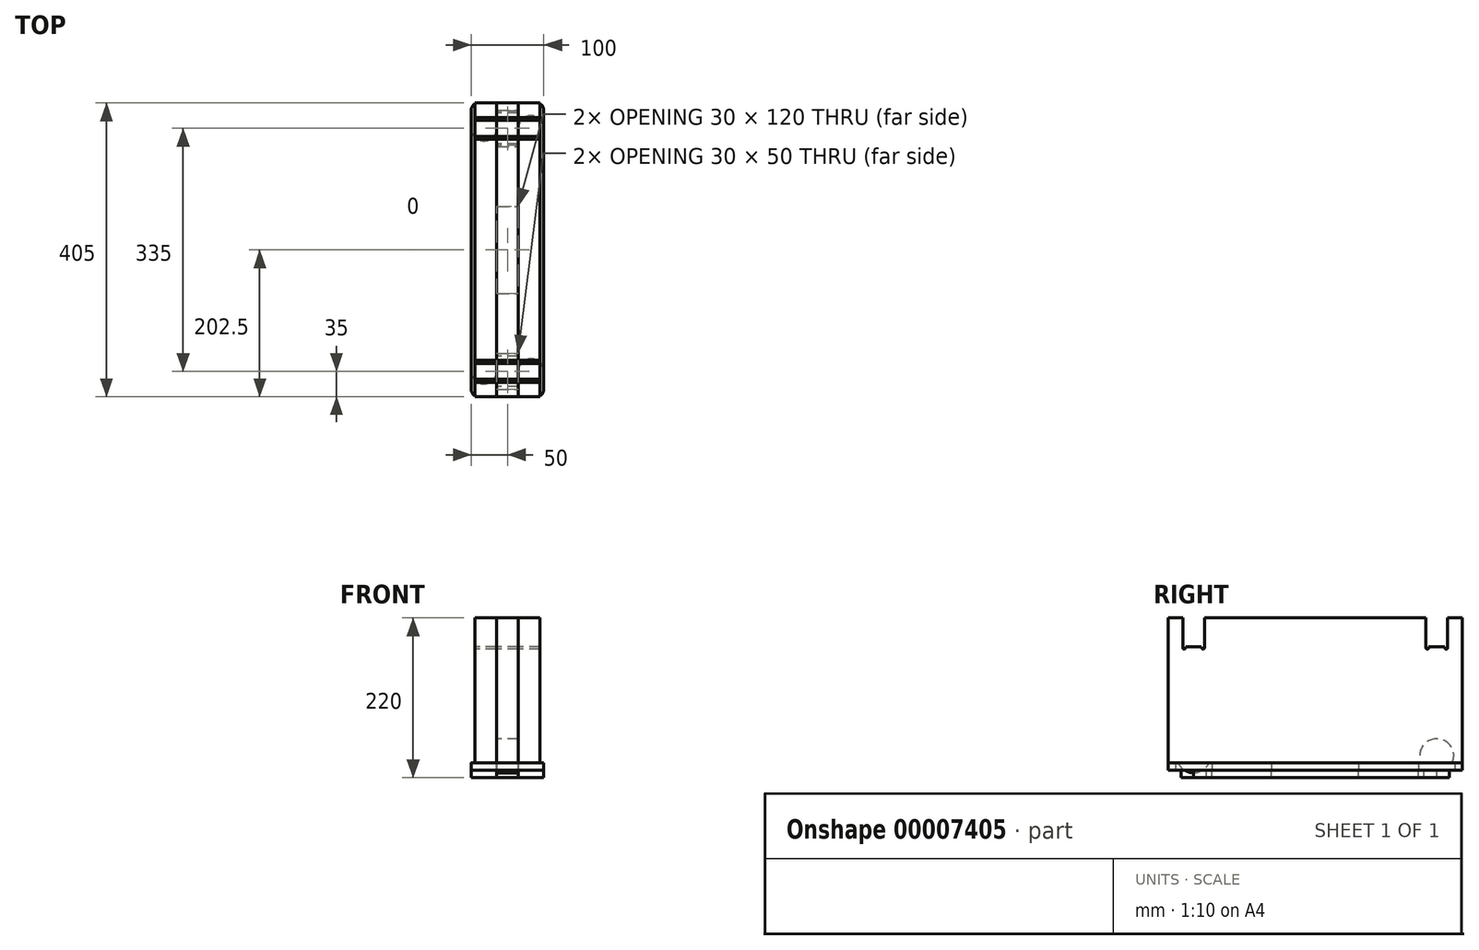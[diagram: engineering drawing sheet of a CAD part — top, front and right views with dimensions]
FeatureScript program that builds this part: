
annotation { "Feature Type Name" : "Feature", "Feature Type Description" : "" }
export const myFeature = defineFeature(function(context is Context, id is Id, definition is map)
    precondition{}
    {
        {
            var Q0;
            Q0=qCreatedBy(makeId("Top.planeOp"),FACE);
            var sketch = newSketch(context, id + "F0", { "sketchPlane" : qUnion([Q0])});
            skLineSegment(sketch, "E0.bottom", {"start": v(10, 0) * mm, "end": v(90, 0) * mm});
            skLineSegment(sketch, "E0.top", {"start": v(10, 405) * mm, "end": v(90, 405) * mm});
            skLineSegment(sketch, "E0.left", {"start": v(0, 10) * mm, "end": v(0, 395) * mm});
            skLineSegment(sketch, "E0.right", {"start": v(100, 10) * mm, "end": v(100, 395) * mm});
            skLineSegment(sketch, "E1", {"start": v(35, 0) * mm, "end": v(35, 405) * mm, "construction": true});
            skLineSegment(sketch, "E2", {"start": v(65, 0) * mm, "end": v(65, 405) * mm, "construction": true});
            skLineSegment(sketch, "E3", {"start": v(0, 202.5) * mm, "end": v(35, 202.5) * mm, "construction": true});
            skLineSegment(sketch, "E4", {"start": v(65, 202.5) * mm, "end": v(100, 202.5) * mm, "construction": true});
            skLineSegment(sketch, "E5.bottom", {"start": v(37, 395) * mm, "end": v(63, 395) * mm});
            skLineSegment(sketch, "E5.top", {"start": v(37, 345) * mm, "end": v(63, 345) * mm});
            skLineSegment(sketch, "E5.left", {"start": v(35, 393) * mm, "end": v(35, 347) * mm});
            skLineSegment(sketch, "E5.right", {"start": v(65, 393) * mm, "end": v(65, 347) * mm});
            skLineSegment(sketch, "E6", {"start": v(35, 202.5) * mm, "end": v(35, 260.5) * mm});
            skLineSegment(sketch, "E7", {"start": v(37, 262.5) * mm, "end": v(63, 262.5) * mm});
            skLineSegment(sketch, "E8", {"start": v(65, 260.5) * mm, "end": v(65, 202.5) * mm});
            skPoint(sketch, "E9.visualSharp", {"position": v(35, 395) * mm});
            skArc(sketch, "E9.filletArc", {"start": v(37, 395) * mm, "mid": v(35.59, 394.41) * mm, "end": v(35, 393) * mm});
            skPoint(sketch, "E10.visualSharp", {"position": v(35, 345) * mm});
            skArc(sketch, "E10.filletArc", {"start": v(35, 347) * mm, "mid": v(35.59, 345.59) * mm, "end": v(37, 345) * mm});
            skPoint(sketch, "E11.visualSharp", {"position": v(65, 395) * mm});
            skArc(sketch, "E11.filletArc", {"start": v(65, 393) * mm, "mid": v(64.41, 394.41) * mm, "end": v(63, 395) * mm});
            skPoint(sketch, "E12.visualSharp", {"position": v(65, 345) * mm});
            skArc(sketch, "E12.filletArc", {"start": v(63, 345) * mm, "mid": v(64.41, 345.59) * mm, "end": v(65, 347) * mm});
            skPoint(sketch, "E13.visualSharp", {"position": v(35, 262.5) * mm});
            skArc(sketch, "E13.filletArc", {"start": v(37, 262.5) * mm, "mid": v(35.59, 261.91) * mm, "end": v(35, 260.5) * mm});
            skPoint(sketch, "E14.visualSharp", {"position": v(65, 262.5) * mm});
            skArc(sketch, "E14.filletArc", {"start": v(65, 260.5) * mm, "mid": v(64.41, 261.91) * mm, "end": v(63, 262.5) * mm});
            skArc(sketch, "E15.0.MirrorCS", {"start": v(63, 60) * mm, "mid": v(64.41, 59.41) * mm, "end": v(65, 58) * mm});
            skArc(sketch, "E15.1.MirrorCS", {"start": v(65, 144.5) * mm, "mid": v(64.41, 143.09) * mm, "end": v(63, 142.5) * mm});
            skArc(sketch, "E15.2.MirrorCS", {"start": v(37, 10) * mm, "mid": v(35.59, 10.59) * mm, "end": v(35, 12) * mm});
            skArc(sketch, "E15.3.MirrorCS", {"start": v(35, 58) * mm, "mid": v(35.59, 59.41) * mm, "end": v(37, 60) * mm});
            skArc(sketch, "E15.4.MirrorCS", {"start": v(37, 142.5) * mm, "mid": v(35.59, 143.09) * mm, "end": v(35, 144.5) * mm});
            skArc(sketch, "E15.5.MirrorCS", {"start": v(65, 12) * mm, "mid": v(64.41, 10.59) * mm, "end": v(63, 10) * mm});
            skPoint(sketch, "E15.6.MirrorP", {"position": v(65, 10) * mm});
            skLineSegment(sketch, "E15.7.MirrorCS", {"start": v(37, 142.5) * mm, "end": v(63, 142.5) * mm});
            skPoint(sketch, "E15.8.MirrorP", {"position": v(35, 10) * mm});
            skLineSegment(sketch, "E15.9.MirrorCS", {"start": v(35, 12) * mm, "end": v(35, 58) * mm});
            skPoint(sketch, "E15.10.MirrorP", {"position": v(65, 142.5) * mm});
            skLineSegment(sketch, "E15.11.MirrorCS", {"start": v(37, 60) * mm, "end": v(63, 60) * mm});
            skLineSegment(sketch, "E15.12.MirrorCS", {"start": v(37, 10) * mm, "end": v(63, 10) * mm});
            skLineSegment(sketch, "E15.13.MirrorCS", {"start": v(65, 12) * mm, "end": v(65, 58) * mm});
            skPoint(sketch, "E15.14.MirrorP", {"position": v(35, 142.5) * mm});
            skPoint(sketch, "E15.15.MirrorP", {"position": v(35, 60) * mm});
            skPoint(sketch, "E15.16.MirrorP", {"position": v(65, 60) * mm});
            skLineSegment(sketch, "E16.0.MirrorCS", {"start": v(35, 202.5) * mm, "end": v(35, 144.5) * mm});
            skLineSegment(sketch, "E17.0.MirrorCS", {"start": v(65, 144.5) * mm, "end": v(65, 202.5) * mm});
            skPoint(sketch, "E18.visualSharp", {"position": v(0, 405) * mm});
            skArc(sketch, "E18.filletArc", {"start": v(10, 405) * mm, "mid": v(2.93, 402.07) * mm, "end": v(0, 395) * mm});
            skPoint(sketch, "E19.visualSharp", {"position": v(100, 405) * mm});
            skArc(sketch, "E19.filletArc", {"start": v(100, 395) * mm, "mid": v(97.07, 402.07) * mm, "end": v(90, 405) * mm});
            skPoint(sketch, "E20.visualSharp", {"position": v(100, 0) * mm});
            skArc(sketch, "E20.filletArc", {"start": v(90, 0) * mm, "mid": v(97.07, 2.93) * mm, "end": v(100, 10) * mm});
            skPoint(sketch, "E21.visualSharp", {"position": v(0, 0) * mm});
            skArc(sketch, "E21.filletArc", {"start": v(0, 10) * mm, "mid": v(2.93, 2.93) * mm, "end": v(10, 0) * mm});
            skSolve(sketch);
        }
        {
            var Q0;
            Q0=makeQuery(id+"F0.imprint","IMPRINT",FACE,{"disambiguationData":[TD([[makeQuery(id+"F0.imprint","IMPRINT",EDGE,{"derivedFrom":sQuery(id+"F0.wireOp",EDGE,"E0.bottom")}),1.0]])]});
            extrude(context, id + "F1", {"entities" : qUnion([Q0]), "depth" : 10 * mm});
        }
        {
            var Q0;
            Q0=makeQuery(id+"F1.opExtrude","CAP_FACE",FACE,{"disambiguationData":[OSD([sQuery(id+"F0.wireOp",EDGE,"E0.bottom"),sQuery(id+"F0.wireOp",EDGE,"E0.top"),sQuery(id+"F0.wireOp",EDGE,"E0.left"),sQuery(id+"F0.wireOp",EDGE,"E0.right"),sQuery(id+"F0.wireOp",EDGE,"E5.bottom"),sQuery(id+"F0.wireOp",EDGE,"E5.top"),sQuery(id+"F0.wireOp",EDGE,"E5.left"),sQuery(id+"F0.wireOp",EDGE,"E5.right"),sQuery(id+"F0.wireOp",EDGE,"E6"),sQuery(id+"F0.wireOp",EDGE,"E7"),sQuery(id+"F0.wireOp",EDGE,"E8"),sQuery(id+"F0.wireOp",EDGE,"E9.filletArc"),sQuery(id+"F0.wireOp",EDGE,"E10.filletArc"),sQuery(id+"F0.wireOp",EDGE,"E11.filletArc"),sQuery(id+"F0.wireOp",EDGE,"E12.filletArc"),sQuery(id+"F0.wireOp",EDGE,"E13.filletArc"),sQuery(id+"F0.wireOp",EDGE,"E14.filletArc"),sQuery(id+"F0.wireOp",EDGE,"E15.0.MirrorCS"),sQuery(id+"F0.wireOp",EDGE,"E15.1.MirrorCS"),sQuery(id+"F0.wireOp",EDGE,"E15.2.MirrorCS"),sQuery(id+"F0.wireOp",EDGE,"E15.3.MirrorCS"),sQuery(id+"F0.wireOp",EDGE,"E15.4.MirrorCS"),sQuery(id+"F0.wireOp",EDGE,"E15.5.MirrorCS"),sQuery(id+"F0.wireOp",EDGE,"E15.7.MirrorCS"),sQuery(id+"F0.wireOp",EDGE,"E15.9.MirrorCS"),sQuery(id+"F0.wireOp",EDGE,"E15.11.MirrorCS"),sQuery(id+"F0.wireOp",EDGE,"E15.12.MirrorCS"),sQuery(id+"F0.wireOp",EDGE,"E15.13.MirrorCS"),sQuery(id+"F0.wireOp",EDGE,"E16.0.MirrorCS"),sQuery(id+"F0.wireOp",EDGE,"E17.0.MirrorCS"),sQuery(id+"F0.wireOp",EDGE,"E18.filletArc"),sQuery(id+"F0.wireOp",EDGE,"E19.filletArc"),sQuery(id+"F0.wireOp",EDGE,"E20.filletArc"),sQuery(id+"F0.wireOp",EDGE,"E21.filletArc")])],"isStart":false});
            var sketch = newSketch(context, id + "F2", { "sketchPlane" : qUnion([Q0])});
            skLineSegment(sketch, "E22.bottom", {"start": v(35, 0) * mm, "end": v(5, 0) * mm});
            skLineSegment(sketch, "E22.top", {"start": v(35, 405) * mm, "end": v(5, 405) * mm});
            skLineSegment(sketch, "E22.left", {"start": v(35, 0) * mm, "end": v(35, 405) * mm});
            skLineSegment(sketch, "E22.right", {"start": v(5, 0) * mm, "end": v(5, 405) * mm});
            skLineSegment(sketch, "E23.bottom", {"start": v(65, 0) * mm, "end": v(95, 0) * mm});
            skLineSegment(sketch, "E23.top", {"start": v(65, 405) * mm, "end": v(95, 405) * mm});
            skLineSegment(sketch, "E23.left", {"start": v(65, 0) * mm, "end": v(65, 405) * mm});
            skLineSegment(sketch, "E23.right", {"start": v(95, 0) * mm, "end": v(95, 405) * mm});
            skSolve(sketch);
        }
        {
            var Q0;
            {var subQ9=sQuery(id+"F2.wireOp",EDGE,"E22.left");var subQ12=makeQuery(id+"F2.imprint","INTERSECT",VERTEX,{"derivedFrom":[makeQuery(id+"F1.opExtrude","CAP_EDGE",EDGE,{"disambiguationData":[OSD([sQuery(id+"F0.wireOp",EDGE,"E13.filletArc")])],"isStart":false}),subQ9]});var subQ16=makeQuery(id+"F2.imprint","INTERSECT",VERTEX,{"derivedFrom":[makeQuery(id+"F1.opExtrude","CAP_EDGE",EDGE,{"disambiguationData":[OSD([sQuery(id+"F0.wireOp",EDGE,"E15.4.MirrorCS")])],"isStart":false}),subQ9]});Q0=makeQuery(id+"F2.imprint","IMPRINT",FACE,{"disambiguationData":[TD([[makeQuery(id+"F2.imprint","IMPRINT",EDGE,{"disambiguationData":[TD([[subQ12,-1.0],[subQ16,1.0]])],"derivedFrom":subQ9}),-1.0]])]});}
            var Q1;
            {var subQ7=sQuery(id+"F2.wireOp",EDGE,"E23.left");var subQ9=makeQuery(id+"F2.imprint","INTERSECT",VERTEX,{"derivedFrom":[makeQuery(id+"F1.opExtrude","CAP_EDGE",EDGE,{"disambiguationData":[OSD([sQuery(id+"F0.wireOp",EDGE,"E11.filletArc")])],"isStart":false}),subQ7]});var subQ11=makeQuery(id+"F2.imprint","INTERSECT",VERTEX,{"derivedFrom":[makeQuery(id+"F1.opExtrude","CAP_EDGE",EDGE,{"disambiguationData":[OSD([sQuery(id+"F0.wireOp",EDGE,"E12.filletArc")])],"isStart":false}),subQ7]});Q1=makeQuery(id+"F2.imprint","IMPRINT",FACE,{"disambiguationData":[TD([[makeQuery(id+"F2.imprint","IMPRINT",EDGE,{"disambiguationData":[TD([[subQ9,-1.0],[subQ11,1.0]])],"derivedFrom":subQ7}),1.0]])]});}
            var Q2;
            {var subQ0=makeQuery(id+"F1.opExtrude","CAP_EDGE",EDGE,{"disambiguationData":[OSD([sQuery(id+"F0.wireOp",EDGE,"E20.filletArc")])],"isStart":false});var subQ3=sQuery(id+"F2.wireOp",EDGE,"E23.bottom");var subQ4=makeQuery(id+"F2.imprint","INTERSECT",VERTEX,{"derivedFrom":[subQ0,subQ3]});Q2=makeQuery(id+"F2.imprint","IMPRINT",FACE,{"disambiguationData":[TD([[makeQuery(id+"F2.imprint","IMPRINT",EDGE,{"disambiguationData":[TD([[subQ4,-1.0]])],"derivedFrom":subQ3}),1.0]])]});}
            var Q3;
            {var subQ1=sQuery(id+"F2.wireOp",EDGE,"E22.right");var subQ3=sQuery(id+"F2.wireOp",EDGE,"E22.bottom");var subQ5=makeQuery(id+"F2.imprint","INTERSECT",VERTEX,{"derivedFrom":[subQ3,subQ1]});Q3=makeQuery(id+"F2.imprint","IMPRINT",FACE,{"disambiguationData":[TD([[makeQuery(id+"F2.imprint","IMPRINT",EDGE,{"disambiguationData":[TD([[subQ5,1.0]])],"derivedFrom":subQ3}),-1.0]])]});}
            var Q4;
            {var subQ0=makeQuery(id+"F1.opExtrude","CAP_EDGE",EDGE,{"disambiguationData":[OSD([sQuery(id+"F0.wireOp",EDGE,"E19.filletArc")])],"isStart":false});var subQ3=sQuery(id+"F2.wireOp",EDGE,"E23.top");var subQ4=makeQuery(id+"F2.imprint","INTERSECT",VERTEX,{"derivedFrom":[subQ0,subQ3]});Q4=makeQuery(id+"F2.imprint","IMPRINT",FACE,{"disambiguationData":[TD([[makeQuery(id+"F2.imprint","IMPRINT",EDGE,{"disambiguationData":[TD([[subQ4,-1.0]])],"derivedFrom":subQ3}),-1.0]])]});}
            var Q5;
            {var subQ1=sQuery(id+"F2.wireOp",EDGE,"E22.right");var subQ3=sQuery(id+"F2.wireOp",EDGE,"E22.top");var subQ5=makeQuery(id+"F2.imprint","INTERSECT",VERTEX,{"derivedFrom":[subQ3,subQ1]});Q5=makeQuery(id+"F2.imprint","IMPRINT",FACE,{"disambiguationData":[TD([[makeQuery(id+"F2.imprint","IMPRINT",EDGE,{"disambiguationData":[TD([[subQ5,1.0]])],"derivedFrom":subQ3}),1.0]])]});}
            extrude(context, id + "F3", {"entities" : qUnion([Q0, Q1, Q2, Q3, Q4, Q5]), "depth" : 200 * mm});
        }
        {
            var Q0;
            Q0=makeQuery(id+"F3.opExtrude","SWEPT_FACE",FACE,{"disambiguationData":[OSD([sQuery(id+"F2.wireOp",EDGE,"E22.left")])]});
            var sketch = newSketch(context, id + "F4", { "sketchPlane" : qUnion([Q0])});
            skCircle(sketch, "E24", {"center": v(35, 20) * mm, "radius": 23.5 * mm});
            skLineSegment(sketch, "E25.0", {"start": v(12, 10) * mm, "end": v(58, 10) * mm, "construction": true});
            skLineSegment(sketch, "E26", {"start": v(35, 20) * mm, "end": v(35, 10) * mm, "construction": true});
            skLineSegment(sketch, "E27", {"start": v(202.5, 10) * mm, "end": v(202.5, 210) * mm, "construction": true});
            skCircle(sketch, "E28.0.MirrorC", {"center": v(370, 20) * mm, "radius": 23.5 * mm});
            skSolve(sketch);
        }
        {
            var Q0;
            {var subQ0=makeQuery(id+"F3.opExtrude","CAP_EDGE",EDGE,{"disambiguationData":[OSD([sQuery(id+"F2.wireOp",EDGE,"E22.left")])],"isStart":true});var subQ1=sQuery(id+"F4.wireOp",EDGE,"E24");var subQ3=makeQuery(id+"F4.imprint","INTERSECT",VERTEX,{"disambiguationData":[OD(0.0)],"derivedFrom":[subQ0,subQ1]});Q0=makeQuery(id+"F4.imprint","IMPRINT",FACE,{"disambiguationData":[TD([[makeQuery(id+"F4.imprint","IMPRINT",EDGE,{"disambiguationData":[TD([[subQ3,1.0]])],"derivedFrom":subQ1}),1.0]])]});}
            var Q1;
            {var subQ0=makeQuery(id+"F3.opExtrude","CAP_EDGE",EDGE,{"disambiguationData":[OSD([sQuery(id+"F2.wireOp",EDGE,"E22.left")])],"isStart":true});var subQ1=sQuery(id+"F4.wireOp",EDGE,"E28.0.MirrorC");var subQ3=makeQuery(id+"F4.imprint","INTERSECT",VERTEX,{"disambiguationData":[OD(0.0)],"derivedFrom":[subQ0,subQ1]});Q1=makeQuery(id+"F4.imprint","IMPRINT",FACE,{"disambiguationData":[TD([[makeQuery(id+"F4.imprint","IMPRINT",EDGE,{"disambiguationData":[TD([[subQ3,1.0]])],"derivedFrom":subQ1}),-1.0]])]});}
            var Q2;
            {var subQ0=makeQuery(id+"F3.opExtrude","CAP_EDGE",EDGE,{"disambiguationData":[OSD([sQuery(id+"F2.wireOp",EDGE,"E22.left")])],"isStart":true});var subQ1=sQuery(id+"F4.wireOp",EDGE,"E24");var subQ3=makeQuery(id+"F4.imprint","INTERSECT",VERTEX,{"disambiguationData":[OD(0.0)],"derivedFrom":[subQ0,subQ1]});Q2=makeQuery(id+"F4.imprint","IMPRINT",FACE,{"disambiguationData":[TD([[makeQuery(id+"F4.imprint","IMPRINT",EDGE,{"disambiguationData":[TD([[subQ3,-1.0]])],"derivedFrom":subQ1}),1.0]])]});}
            var Q3;
            {var subQ0=makeQuery(id+"F3.opExtrude","CAP_EDGE",EDGE,{"disambiguationData":[OSD([sQuery(id+"F2.wireOp",EDGE,"E22.left")])],"isStart":true});var subQ1=sQuery(id+"F4.wireOp",EDGE,"E28.0.MirrorC");var subQ3=makeQuery(id+"F4.imprint","INTERSECT",VERTEX,{"disambiguationData":[OD(0.0)],"derivedFrom":[subQ0,subQ1]});Q3=makeQuery(id+"F4.imprint","IMPRINT",FACE,{"disambiguationData":[TD([[makeQuery(id+"F4.imprint","IMPRINT",EDGE,{"disambiguationData":[TD([[subQ3,-1.0]])],"derivedFrom":subQ1}),-1.0]])]});}
            extrude(context, id + "F5", {"entities" : qUnion([Q0, Q1, Q2, Q3]), "depth" : 30 * mm});
        }
        {
            var Q0;
            Q0=makeQuery(id+"F1.opExtrude","CAP_FACE",FACE,{"disambiguationData":[OSD([sQuery(id+"F0.wireOp",EDGE,"E0.bottom"),sQuery(id+"F0.wireOp",EDGE,"E0.top"),sQuery(id+"F0.wireOp",EDGE,"E0.left"),sQuery(id+"F0.wireOp",EDGE,"E0.right"),sQuery(id+"F0.wireOp",EDGE,"E5.bottom"),sQuery(id+"F0.wireOp",EDGE,"E5.top"),sQuery(id+"F0.wireOp",EDGE,"E5.left"),sQuery(id+"F0.wireOp",EDGE,"E5.right"),sQuery(id+"F0.wireOp",EDGE,"E6"),sQuery(id+"F0.wireOp",EDGE,"E7"),sQuery(id+"F0.wireOp",EDGE,"E8"),sQuery(id+"F0.wireOp",EDGE,"E9.filletArc"),sQuery(id+"F0.wireOp",EDGE,"E10.filletArc"),sQuery(id+"F0.wireOp",EDGE,"E11.filletArc"),sQuery(id+"F0.wireOp",EDGE,"E12.filletArc"),sQuery(id+"F0.wireOp",EDGE,"E13.filletArc"),sQuery(id+"F0.wireOp",EDGE,"E14.filletArc"),sQuery(id+"F0.wireOp",EDGE,"E15.0.MirrorCS"),sQuery(id+"F0.wireOp",EDGE,"E15.1.MirrorCS"),sQuery(id+"F0.wireOp",EDGE,"E15.2.MirrorCS"),sQuery(id+"F0.wireOp",EDGE,"E15.3.MirrorCS"),sQuery(id+"F0.wireOp",EDGE,"E15.4.MirrorCS"),sQuery(id+"F0.wireOp",EDGE,"E15.5.MirrorCS"),sQuery(id+"F0.wireOp",EDGE,"E15.7.MirrorCS"),sQuery(id+"F0.wireOp",EDGE,"E15.9.MirrorCS"),sQuery(id+"F0.wireOp",EDGE,"E15.11.MirrorCS"),sQuery(id+"F0.wireOp",EDGE,"E15.12.MirrorCS"),sQuery(id+"F0.wireOp",EDGE,"E15.13.MirrorCS"),sQuery(id+"F0.wireOp",EDGE,"E16.0.MirrorCS"),sQuery(id+"F0.wireOp",EDGE,"E17.0.MirrorCS"),sQuery(id+"F0.wireOp",EDGE,"E18.filletArc"),sQuery(id+"F0.wireOp",EDGE,"E19.filletArc"),sQuery(id+"F0.wireOp",EDGE,"E20.filletArc"),sQuery(id+"F0.wireOp",EDGE,"E21.filletArc")])],"isStart":true});
            var sketch = newSketch(context, id + "F6", { "sketchPlane" : qUnion([Q0])});
            skLineSegment(sketch, "E29", {"start": v(35, -35) * mm, "end": v(17.5, -35) * mm, "construction": true});
            skLineSegment(sketch, "E30", {"start": v(0, -35) * mm, "end": v(17.5, -35) * mm, "construction": true});
            skCircle(sketch, "E31", {"center": v(17.5, -35) * mm, "radius": 17.5 * mm});
            skLineSegment(sketch, "E32", {"start": v(50, -10) * mm, "end": v(50, -60) * mm, "construction": true});
            skLineSegment(sketch, "E33", {"start": v(0, -202.5) * mm, "end": v(100, -202.5) * mm, "construction": true});
            skCircle(sketch, "E34.0.MirrorC", {"center": v(82.5, -35) * mm, "radius": 17.5 * mm});
            skCircle(sketch, "E35.0.MirrorC", {"center": v(82.5, -370) * mm, "radius": 17.5 * mm});
            skCircle(sketch, "E36.0.MirrorC", {"center": v(17.5, -370) * mm, "radius": 17.5 * mm});
            skSolve(sketch);
        }
        {
            var Q0;
            {var subQ0=sQuery(id+"F6.wireOp",EDGE,"E31");var subQ2=makeQuery(id+"F6.imprint","INTERSECT",VERTEX,{"derivedFrom":[makeQuery(id+"F1.opExtrude","CAP_EDGE",EDGE,{"disambiguationData":[OSD([sQuery(id+"F0.wireOp",EDGE,"E0.left")])],"isStart":true}),subQ0]});Q0=makeQuery(id+"F6.imprint","IMPRINT",FACE,{"disambiguationData":[TD([[makeQuery(id+"F6.imprint","IMPRINT",EDGE,{"disambiguationData":[TD([[subQ2,1.0]])],"derivedFrom":subQ0}),1.0]])]});}
            var Q1;
            {var subQ0=sQuery(id+"F6.wireOp",EDGE,"E34.0.MirrorC");var subQ2=makeQuery(id+"F6.imprint","INTERSECT",VERTEX,{"derivedFrom":[makeQuery(id+"F1.opExtrude","CAP_EDGE",EDGE,{"disambiguationData":[OSD([sQuery(id+"F0.wireOp",EDGE,"E0.right")])],"isStart":true}),subQ0]});Q1=makeQuery(id+"F6.imprint","IMPRINT",FACE,{"disambiguationData":[TD([[makeQuery(id+"F6.imprint","IMPRINT",EDGE,{"disambiguationData":[TD([[subQ2,1.0]])],"derivedFrom":subQ0}),-1.0]])]});}
            var Q2;
            {var subQ0=sQuery(id+"F6.wireOp",EDGE,"E35.0.MirrorC");var subQ2=makeQuery(id+"F6.imprint","INTERSECT",VERTEX,{"derivedFrom":[makeQuery(id+"F1.opExtrude","CAP_EDGE",EDGE,{"disambiguationData":[OSD([sQuery(id+"F0.wireOp",EDGE,"E0.right")])],"isStart":true}),subQ0]});Q2=makeQuery(id+"F6.imprint","IMPRINT",FACE,{"disambiguationData":[TD([[makeQuery(id+"F6.imprint","IMPRINT",EDGE,{"disambiguationData":[TD([[subQ2,1.0]])],"derivedFrom":subQ0}),1.0]])]});}
            var Q3;
            {var subQ0=sQuery(id+"F6.wireOp",EDGE,"E36.0.MirrorC");var subQ2=makeQuery(id+"F6.imprint","INTERSECT",VERTEX,{"derivedFrom":[makeQuery(id+"F1.opExtrude","CAP_EDGE",EDGE,{"disambiguationData":[OSD([sQuery(id+"F0.wireOp",EDGE,"E0.left")])],"isStart":true}),subQ0]});Q3=makeQuery(id+"F6.imprint","IMPRINT",FACE,{"disambiguationData":[TD([[makeQuery(id+"F6.imprint","IMPRINT",EDGE,{"disambiguationData":[TD([[subQ2,1.0]])],"derivedFrom":subQ0}),-1.0]])]});}
            extrude(context, id + "F7", {"entities" : qUnion([Q0, Q1, Q2, Q3]), "depth" : 10 * mm});
        }
        {
            var Q0;
            Q0=makeQuery(id+"F3.opExtrude","SWEPT_FACE",FACE,{"disambiguationData":[OSD([sQuery(id+"F2.wireOp",EDGE,"E22.right")])]});
            var sketch = newSketch(context, id + "F8", { "sketchPlane" : qUnion([Q0])});
            skLineSegment(sketch, "E37", {"start": v(-202.5, 210) * mm, "end": v(-202.5, 10) * mm, "construction": true});
            skLineSegment(sketch, "E38.bottom", {"start": v(-385, 210) * mm, "end": v(-355, 210) * mm});
            skLineSegment(sketch, "E38.top", {"start": v(-385, 170) * mm, "end": v(-355, 170) * mm});
            skLineSegment(sketch, "E38.left", {"start": v(-385, 210) * mm, "end": v(-385, 170) * mm});
            skLineSegment(sketch, "E38.right", {"start": v(-355, 210) * mm, "end": v(-355, 170) * mm});
            skLineSegment(sketch, "E39", {"start": v(-385, 170) * mm, "end": v(-385, 169) * mm});
            skLineSegment(sketch, "E40", {"start": v(-370, 210) * mm, "end": v(-370, 170) * mm, "construction": true});
            skLineSegment(sketch, "E41", {"start": v(-381, 170) * mm, "end": v(-381, 169) * mm});
            skArc(sketch, "E42", {"start": v(-385, 169) * mm, "mid": v(-383, 167) * mm, "end": v(-381, 169) * mm});
            skLineSegment(sketch, "E43.0.MirrorCS", {"start": v(-359, 170) * mm, "end": v(-359, 169) * mm});
            skLineSegment(sketch, "E43.1.MirrorCS", {"start": v(-355, 170) * mm, "end": v(-355, 169) * mm});
            skArc(sketch, "E43.2.MirrorCS", {"start": v(-355, 169) * mm, "mid": v(-357, 167) * mm, "end": v(-359, 169) * mm});
            skLineSegment(sketch, "E44.0.MirrorCS", {"start": v(-50, 170) * mm, "end": v(-50, 169) * mm});
            skLineSegment(sketch, "E44.1.MirrorCS", {"start": v(-20, 170) * mm, "end": v(-20, 169) * mm});
            skLineSegment(sketch, "E44.2.MirrorCS", {"start": v(-24, 170) * mm, "end": v(-24, 169) * mm});
            skLineSegment(sketch, "E44.3.MirrorCS", {"start": v(-46, 170) * mm, "end": v(-46, 169) * mm});
            skArc(sketch, "E44.4.MirrorCS", {"start": v(-50, 169) * mm, "mid": v(-48, 167) * mm, "end": v(-46, 169) * mm});
            skArc(sketch, "E44.5.MirrorCS", {"start": v(-20, 169) * mm, "mid": v(-22, 167) * mm, "end": v(-24, 169) * mm});
            skLineSegment(sketch, "E44.6.MirrorCS", {"start": v(-50, 210) * mm, "end": v(-50, 170) * mm});
            skLineSegment(sketch, "E44.7.MirrorCS", {"start": v(-20, 210) * mm, "end": v(-50, 210) * mm});
            skLineSegment(sketch, "E44.8.MirrorCS", {"start": v(-20, 170) * mm, "end": v(-50, 170) * mm});
            skLineSegment(sketch, "E44.9.MirrorCS", {"start": v(-20, 210) * mm, "end": v(-20, 170) * mm});
            skLineSegment(sketch, "E44.10.MirrorCS", {"start": v(-35, 210) * mm, "end": v(-35, 170) * mm, "construction": true});
            skSolve(sketch);
        }
        {
            var Q0;
            Q0=makeQuery(id+"F8.imprint","IMPRINT",FACE,{"disambiguationData":[TD([[makeQuery(id+"F8.imprint","IMPRINT",EDGE,{"derivedFrom":sQuery(id+"F8.wireOp",EDGE,"E38.bottom")}),1.0]])]});
            var Q1;
            {var subQ1=sQuery(id+"F8.wireOp",EDGE,"E39");Q1=makeQuery(id+"F8.imprint","IMPRINT",FACE,{"disambiguationData":[TD([[makeQuery(id+"F8.imprint","IMPRINT",EDGE,{"derivedFrom":subQ1}),1.0]])]});}
            var Q2;
            {var subQ1=sQuery(id+"F8.wireOp",EDGE,"E43.0.MirrorCS");Q2=makeQuery(id+"F8.imprint","IMPRINT",FACE,{"disambiguationData":[TD([[makeQuery(id+"F8.imprint","IMPRINT",EDGE,{"derivedFrom":subQ1}),1.0]])]});}
            var Q3;
            {var subQ3=sQuery(id+"F8.wireOp",EDGE,"E44.6.MirrorCS");Q3=makeQuery(id+"F8.imprint","IMPRINT",FACE,{"disambiguationData":[TD([[makeQuery(id+"F8.imprint","IMPRINT",EDGE,{"derivedFrom":subQ3}),1.0]])]});}
            var Q4;
            {var subQ2=sQuery(id+"F8.wireOp",EDGE,"E44.0.MirrorCS");Q4=makeQuery(id+"F8.imprint","IMPRINT",FACE,{"disambiguationData":[TD([[makeQuery(id+"F8.imprint","IMPRINT",EDGE,{"derivedFrom":subQ2}),1.0]])]});}
            var Q5;
            {var subQ2=sQuery(id+"F8.wireOp",EDGE,"E44.1.MirrorCS");Q5=makeQuery(id+"F8.imprint","IMPRINT",FACE,{"disambiguationData":[TD([[makeQuery(id+"F8.imprint","IMPRINT",EDGE,{"derivedFrom":subQ2}),-1.0]])]});}
            var Q6;
            Q6=makeQuery(id+"F3.opExtrude","SWEPT_FACE",FACE,{"disambiguationData":[OSD([sQuery(id+"F2.wireOp",EDGE,"E23.right")])]});
            extrude(context, id + "F9", {"entities" : qUnion([Q0, Q1, Q2, Q3, Q4, Q5]), "operationType" : NewBodyOperationType.REMOVE, "endBound" : BoundingType.UP_TO_SURFACE, "oppositeDirection" : true, "endBoundEntityFace" : qUnion([Q6]), "depth" : 25 * mm});
        }
    });
